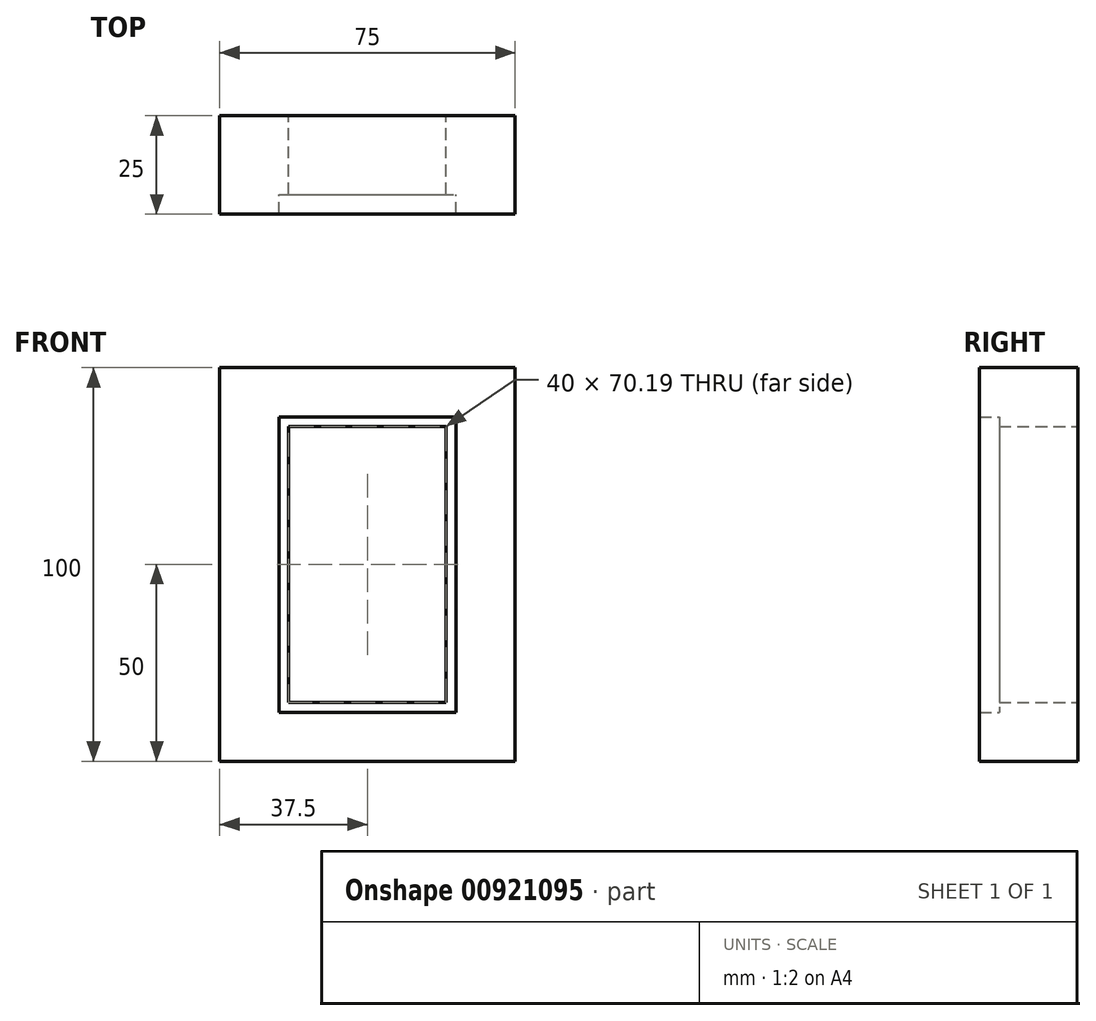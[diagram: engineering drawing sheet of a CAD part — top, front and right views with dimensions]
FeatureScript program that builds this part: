
annotation { "Feature Type Name" : "Feature", "Feature Type Description" : "" }
export const myFeature = defineFeature(function(context is Context, id is Id, definition is map)
    precondition{}
    {
        {
            var Q0;
            Q0=qCreatedBy(makeId("Front.planeOp"),FACE);
            var sketch = newSketch(context, id + "F0", { "sketchPlane" : qUnion([Q0])});
            skLineSegment(sketch, "E0.bottom", {"start": v(-22.5, 37.4) * mm, "end": v(22.5, 37.4) * mm});
            skLineSegment(sketch, "E0.top", {"start": v(-22.5, -37.6) * mm, "end": v(22.5, -37.6) * mm});
            skLineSegment(sketch, "E0.left", {"start": v(-22.5, 37.4) * mm, "end": v(-22.5, -37.6) * mm});
            skLineSegment(sketch, "E0.right", {"start": v(22.5, 37.4) * mm, "end": v(22.5, -37.6) * mm});
            skPoint(sketch, "E0.middle", {"position": v(0, -0.1) * mm});
            skPoint(sketch, "E1.0", {"position": v(0, 0) * mm});
            skSolve(sketch);
        }
        {
            var Q0;
            Q0 = qSketchRegion(id + "F0", true);
            var sketch = newSketch(context, id + "F1", { "sketchPlane" : qUnion([Q0])});
            skLineSegment(sketch, "E2.bottom", {"start": v(-20, 35.1) * mm, "end": v(20, 35.1) * mm});
            skLineSegment(sketch, "E2.top", {"start": v(-20, -35.1) * mm, "end": v(20, -35.1) * mm});
            skLineSegment(sketch, "E2.left", {"start": v(-20, 35.1) * mm, "end": v(-20, -35.1) * mm});
            skLineSegment(sketch, "E2.right", {"start": v(20, 35.1) * mm, "end": v(20, -35.1) * mm});
            skPoint(sketch, "E2.middle", {"position": v(0, 0) * mm});
            skSolve(sketch);
        }
        {
            var Q0;
            Q0 = qSketchRegion(id + "F0", true);
            var sketch = newSketch(context, id + "F2", { "sketchPlane" : qUnion([Q0])});
            skLineSegment(sketch, "E3.bottom", {"start": v(37.5, 50) * mm, "end": v(-37.5, 50) * mm});
            skLineSegment(sketch, "E3.top", {"start": v(37.5, -50) * mm, "end": v(-37.5, -50) * mm});
            skLineSegment(sketch, "E3.left", {"start": v(37.5, 50) * mm, "end": v(37.5, -50) * mm});
            skLineSegment(sketch, "E3.right", {"start": v(-37.5, 50) * mm, "end": v(-37.5, -50) * mm});
            skPoint(sketch, "E3.middle", {"position": v(0, 0) * mm});
            skSolve(sketch);
        }
        {
            var Q0;
            Q0=makeQuery(id+"F1.imprint","IMPRINT",FACE,{"disambiguationData":[TD([[makeQuery(id+"F1.imprint","IMPRINT",EDGE,{"derivedFrom":sQuery(id+"F1.wireOp",EDGE,"E2.bottom")}),1.0]])]});
            extrude(context, id + "F3", {"entities" : qUnion([Q0]), "depth" : 20 * mm, "offsetDistance" : 25 * mm});
        }
        {
            var Q0;
            Q0=makeQuery(id+"F2.imprint","IMPRINT",FACE,{"disambiguationData":[TD([[makeQuery(id+"F2.imprint","IMPRINT",EDGE,{"derivedFrom":sQuery(id+"F2.wireOp",EDGE,"E3.bottom")}),1.0]])]});
            extrude(context, id + "F4", {"entities" : qUnion([Q0]), "operationType" : NewBodyOperationType.ADD, "depth" : 25 * mm, "offsetDistance" : 25 * mm});
        }
    });
